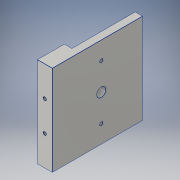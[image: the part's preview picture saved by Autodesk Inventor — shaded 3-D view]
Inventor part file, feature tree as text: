
AUTODESK INVENTOR PART (.ipt)
format: ipt  version: 2016 (Build 200138000, 138)  size: 157,696 bytes
history: native  units: in
note: dims shown in document units (in); Inventor stores cm internally (conversion verified against a paired STEP export)
features: thread x4, extrude x3, sketch x3, chamfer x1
ambient origin geometry x8: Origin, YZ Plane, XZ Plane, XY Plane, X Axis, Y Axis, Z Axis, Center Point
bodies: Solid1 (feature_tree)
feature tree (11):
  extrude  "Extrusion1"  Depth=0.9in
  extrude  "Extrusion2"  Depth=3.0in
  extrude  "Extrusion3"  Depth=0.25in
  chamfer  "Chamfer1"  Distance=1.625in
  thread  "Thread1"  [1 undecoded]
  thread  "Thread2"  [1 undecoded]
  thread  "Thread3"  [1 undecoded]
  thread  "Thread4"  [1 undecoded]
  sketch  "Sketch1"  dims[d0=0.5in d1=0.9in]
  sketch  "Sketch2"  dims[d2=0.25in d3=3.0in]
  sketch  "Sketch3"  dims[d4=3.0in d5=0.0in d6=1.5in d7=1.625in d8=0.3in d9=0.5in d10=0.0in d12=0.1in d13=0.7874in d15=360.0deg d17=1.625in d18=0.005in d19=0.125in d20=45.0deg d21=1.0in d22=0.0in d23=1.0in d24=0.0in d25=0.1in d26=0.1in d27=1.0in d28=1.0in d29=0.25in d30=0.0in d31=1.0in d32=0.0in d33=1.0in d34=0.0in d35=1.812in]
note: 4 required parameter values undecoded (feature->parameter linkage not recoverable at this tier; creation-order binding heuristic only, values carry confidence <= 0.55)
